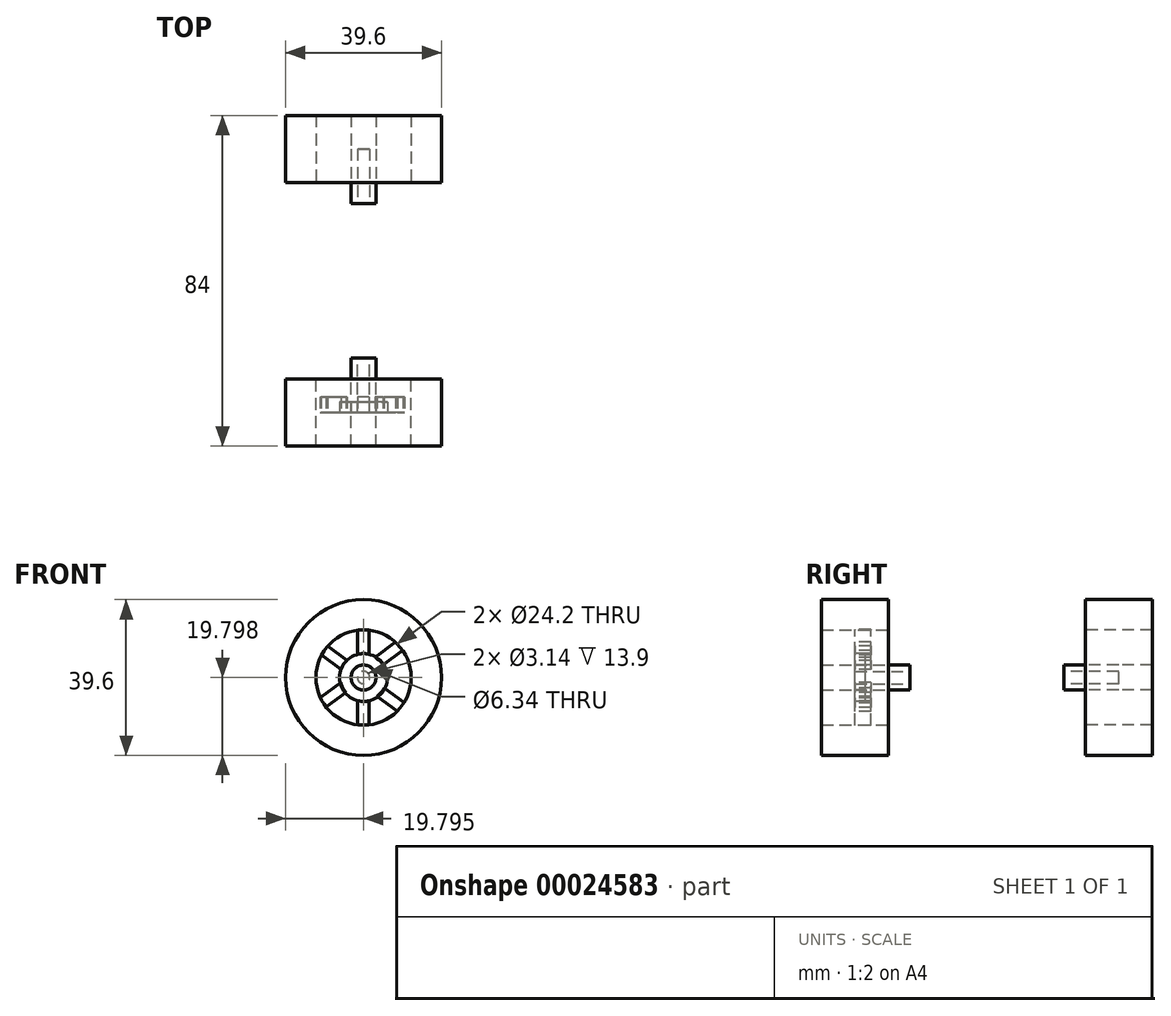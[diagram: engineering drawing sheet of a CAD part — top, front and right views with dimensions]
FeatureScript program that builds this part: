
annotation { "Feature Type Name" : "Feature", "Feature Type Description" : "" }
export const myFeature = defineFeature(function(context is Context, id is Id, definition is map)
    precondition{}
    {
        {
            var Q0;
            Q0=qCreatedBy(makeId("Front.planeOp"),FACE);
            var sketch = newSketch(context, id + "F0", { "sketchPlane" : qUnion([Q0])});
            skCircle(sketch, "E0", {"center": v(-14.5, -5.85) * mm, "radius": 3.17 * mm});
            skCircle(sketch, "E1.0", {"center": v(-14.5, -5.85) * mm, "radius": 1.57 * mm});
            skSolve(sketch);
        }
        {
            var Q0;
            Q0=makeQuery(id+"F0.imprint","IMPRINT",FACE,{"disambiguationData":[TD([[makeQuery(id+"F0.imprint","IMPRINT",EDGE,{"derivedFrom":sQuery(id+"F0.wireOp",EDGE,"E0")}),1.0]])]});
            extrude(context, id + "F1", {"entities" : qUnion([Q0]), "depth" : 9.2 * mm});
        }
        {
            var Q0;
            Q0=makeQuery(id+"F1.opExtrude","CAP_FACE",FACE,{"disambiguationData":[OSD([sQuery(id+"F0.wireOp",EDGE,"E0"),sQuery(id+"F0.wireOp",EDGE,"E1.0")])],"isStart":false});
            var sketch = newSketch(context, id + "F2", { "sketchPlane" : qUnion([Q0])});
            skCircle(sketch, "E2.0", {"center": v(-14.5, -5.85) * mm, "radius": 6.07 * mm});
            skSolve(sketch);
        }
        {
            var Q0;
            Q0=makeQuery(id+"F2.imprint","IMPRINT",FACE,{"disambiguationData":[TD([[makeQuery(id+"F2.imprint","IMPRINT",EDGE,{"derivedFrom":sQuery(id+"F2.wireOp",EDGE,"E2.0")}),1.0]])]});
            extrude(context, id + "F3", {"entities" : qUnion([Q0]), "oppositeDirection" : true, "depth" : 2.7 * mm});
        }
        {
            var Q0;
            Q0=makeQuery(id+"F3.opExtrude","CAP_FACE",FACE,{"disambiguationData":[OSD([sQuery(id+"F0.wireOp",EDGE,"E0"),sQuery(id+"F2.wireOp",EDGE,"E2.0")])],"isStart":true});
            var sketch = newSketch(context, id + "F4", { "sketchPlane" : qUnion([Q0])});
            skArc(sketch, "E3", {"start": v(-23.66, 2.2) * mm, "mid": v(-24.53, 1.09) * mm, "end": v(-25.26, -0.1) * mm});
            skLineSegment(sketch, "E4", {"start": v(-24.08, -13.4) * mm, "end": v(-19, -9.65) * mm});
            skLineSegment(sketch, "E5.0", {"start": v(-13.15, -18.05) * mm, "end": v(-13.15, -11.58) * mm});
            skLineSegment(sketch, "E6.0", {"start": v(-15.95, -18.05) * mm, "end": v(-15.95, -11.55) * mm});
            skLineSegment(sketch, "E7.0", {"start": v(-4.11, -12.26) * mm, "end": v(-9.23, -8.47) * mm});
            skLineSegment(sketch, "E8.0", {"start": v(-5.85, -14.46) * mm, "end": v(-11.04, -10.62) * mm});
            skLineSegment(sketch, "E9.0", {"start": v(-25.55, -11.01) * mm, "end": v(-20.25, -7.1) * mm});
            skLineSegment(sketch, "E10.trimOffspring", {"start": v(-13.15, -0.13) * mm, "end": v(-13.15, 6.35) * mm});
            skLineSegment(sketch, "E11.trimOffspring", {"start": v(-11.62, -0.72) * mm, "end": v(-6.32, 3.2) * mm});
            skLineSegment(sketch, "E12.trimOffspring", {"start": v(-18.55, -1.59) * mm, "end": v(-23.7, 2.22) * mm});
            skCircle(sketch, "E13", {"center": v(-14.5, -5.85) * mm, "radius": 5.88 * mm});
            skLineSegment(sketch, "E14.trimOffspring", {"start": v(-15.95, -0.15) * mm, "end": v(-15.95, 6.35) * mm});
            skLineSegment(sketch, "E15.trimOffspring", {"start": v(-20.06, -3.95) * mm, "end": v(-25.36, -0.03) * mm});
            skLineSegment(sketch, "E16.trimOffspring", {"start": v(-9.55, -2.67) * mm, "end": v(-4.46, 1.1) * mm});
            skArc(sketch, "E17.trimOffspring", {"start": v(-13.15, 6.27) * mm, "mid": v(-14.55, 6.35) * mm, "end": v(-15.95, 6.26) * mm});
            skArc(sketch, "E18.trimOffspring", {"start": v(-4.46, 1.1) * mm, "mid": v(-5.33, 2.2) * mm, "end": v(-6.32, 3.2) * mm});
            skArc(sketch, "E19.trimOffspring", {"start": v(-5.85, -14.46) * mm, "mid": v(-4.92, -13.4) * mm, "end": v(-4.11, -12.26) * mm});
            skArc(sketch, "E20.trimOffspring", {"start": v(-15.95, -17.97) * mm, "mid": v(-14.55, -18.05) * mm, "end": v(-13.15, -17.98) * mm});
            skArc(sketch, "E21.trimOffspring", {"start": v(-25.55, -11.01) * mm, "mid": v(-24.88, -12.25) * mm, "end": v(-24.08, -13.4) * mm});
            skSolve(sketch);
        }
        {
            var Q0;
            {var subQ0=sQuery(id+"F4.wireOp",EDGE,"E17.trimOffspring");Q0=makeQuery(id+"F4.imprint","IMPRINT",FACE,{"disambiguationData":[TD([[makeQuery(id+"F4.imprint","IMPRINT",EDGE,{"derivedFrom":subQ0}),1.0]])]});}
            var Q1;
            {var subQ2=sQuery(id+"F4.wireOp",EDGE,"E11.trimOffspring");Q1=makeQuery(id+"F4.imprint","IMPRINT",FACE,{"disambiguationData":[TD([[makeQuery(id+"F4.imprint","IMPRINT",EDGE,{"derivedFrom":subQ2}),-1.0]])]});}
            var Q2;
            {var subQ2=sQuery(id+"F4.wireOp",EDGE,"E7.0");Q2=makeQuery(id+"F4.imprint","IMPRINT",FACE,{"disambiguationData":[TD([[makeQuery(id+"F4.imprint","IMPRINT",EDGE,{"derivedFrom":subQ2}),1.0]])]});}
            var Q3;
            {var subQ0=sQuery(id+"F4.wireOp",EDGE,"E20.trimOffspring");Q3=makeQuery(id+"F4.imprint","IMPRINT",FACE,{"disambiguationData":[TD([[makeQuery(id+"F4.imprint","IMPRINT",EDGE,{"derivedFrom":subQ0}),1.0]])]});}
            var Q4;
            {var subQ3=sQuery(id+"F4.wireOp",EDGE,"E3");Q4=makeQuery(id+"F4.imprint","IMPRINT",FACE,{"disambiguationData":[TD([[makeQuery(id+"F4.imprint","IMPRINT",EDGE,{"derivedFrom":subQ3}),1.0]])]});}
            var Q5;
            {var subQ2=sQuery(id+"F4.wireOp",EDGE,"E4");Q5=makeQuery(id+"F4.imprint","IMPRINT",FACE,{"disambiguationData":[TD([[makeQuery(id+"F4.imprint","IMPRINT",EDGE,{"derivedFrom":subQ2}),1.0]])]});}
            extrude(context, id + "F5", {"entities" : qUnion([Q0, Q1, Q2, Q3, Q4, Q5]), "oppositeDirection" : true, "depth" : 4 * mm});
        }
        {
            var Q0;
            Q0=makeQuery(id+"F1.opExtrude","CAP_FACE",FACE,{"disambiguationData":[OSD([sQuery(id+"F0.wireOp",EDGE,"E0"),sQuery(id+"F0.wireOp",EDGE,"E1.0")])],"isStart":false});
            var sketch = newSketch(context, id + "F6", { "sketchPlane" : qUnion([Q0])});
            skCircle(sketch, "E22", {"center": v(-14.5, -5.85) * mm, "radius": 12.1 * mm});
            skCircle(sketch, "E23.0", {"center": v(-14.5, -5.85) * mm, "radius": 19.8 * mm});
            skSolve(sketch);
        }
        {
            var Q0;
            Q0=makeQuery(id+"F6.imprint","IMPRINT",FACE,{"disambiguationData":[TD([[makeQuery(id+"F6.imprint","IMPRINT",EDGE,{"derivedFrom":sQuery(id+"F6.wireOp",EDGE,"E22")}),-1.0]])]});
            extrude(context, id + "F7", {"entities" : qUnion([Q0]), "endBound" : BoundingType.SYMMETRIC, "depth" : 17 * mm});
        }
        {
            var Q0;
            Q0=makeQuery(id+"F1.opExtrude","CAP_FACE",FACE,{"disambiguationData":[OSD([sQuery(id+"F0.wireOp",EDGE,"E0"),sQuery(id+"F0.wireOp",EDGE,"E1.0")])],"isStart":true});
            extrude(context, id + "F8", {"entities" : qUnion([Q0]), "operationType" : NewBodyOperationType.ADD, "depth" : 4.7 * mm});
        }
        {
            var Q0;
            Q0=makeQuery(id+"F1.opExtrude","CAP_FACE",FACE,{"disambiguationData":[OSD([sQuery(id+"F0.wireOp",EDGE,"E0"),sQuery(id+"F0.wireOp",EDGE,"E1.0")])],"isStart":false});
            var sketch = newSketch(context, id + "F9", { "sketchPlane" : qUnion([Q0])});
            skCircle(sketch, "E24", {"center": v(-14.5, -5.85) * mm, "radius": 3.16 * mm});
            skSolve(sketch);
        }
        {
            var Q0;
            Q0=qSketchRegion(id+"F9",true);
            var Q1;
            Q1=makeQuery(id+"F7.opExtrude","CAP_FACE",FACE,{"disambiguationData":[OSD([sQuery(id+"F6.wireOp",EDGE,"E22"),sQuery(id+"F6.wireOp",EDGE,"E23.0")])],"isStart":false});
            extrude(context, id + "F10", {"entities" : qUnion([Q0]), "operationType" : NewBodyOperationType.ADD, "endBound" : BoundingType.UP_TO_SURFACE, "endBoundEntityFace" : qUnion([Q1]), "depth" : 25 * mm});
        }
        {
            var Q0;
            Q0=makeQuery(id+"F10.opExtrude","CAP_FACE",FACE,{"disambiguationData":[OSD([sQuery(id+"F9.wireOp",EDGE,"E24")])],"isStart":false});
            extrude(context, id + "F11", {"entities" : qUnion([Q0]), "operationType" : NewBodyOperationType.ADD, "oppositeDirection" : true, "depth" : 3 * mm});
        }
        {
            var Q0;
            Q0=makeQuery(id+"F7.opExtrude","SWEPT_BODY",BODY,{"disambiguationData":[OSD([sQuery(id+"F6.wireOp",EDGE,"E22"),sQuery(id+"F6.wireOp",EDGE,"E23.0")])]});
            var Q1;
            Q1=makeQuery(id+"F1.opExtrude","SWEPT_BODY",BODY,{"disambiguationData":[OSD([sQuery(id+"F0.wireOp",EDGE,"E0"),sQuery(id+"F0.wireOp",EDGE,"E1.0")])]});
            var Q2;
            Q2=makeQuery(id+"F7.opExtrude","CAP_FACE",FACE,{"disambiguationData":[OSD([sQuery(id+"F6.wireOp",EDGE,"E22"),sQuery(id+"F6.wireOp",EDGE,"E23.0")])],"isStart":true});
            mirror(context, id + "F12", {"entities" : qUnion([Q0, Q1]), "mirrorPlane" : qUnion([Q2])});
        }
        {
            var Q0;
            Q0=makeQuery(id+"F12.opPattern","COPY",BODY,{"derivedFrom":makeQuery(id+"F1.opExtrude","SWEPT_BODY",BODY,{"disambiguationData":[OSD([sQuery(id+"F0.wireOp",EDGE,"E0"),sQuery(id+"F0.wireOp",EDGE,"E1.0")])]}),"instanceName":"1"});
            var Q1;
            Q1=makeQuery(id+"F12.opPattern","COPY",BODY,{"derivedFrom":makeQuery(id+"F7.opExtrude","SWEPT_BODY",BODY,{"disambiguationData":[OSD([sQuery(id+"F6.wireOp",EDGE,"E22"),sQuery(id+"F6.wireOp",EDGE,"E23.0")])]}),"instanceName":"1"});
            var Q2;
            Q2=makeQuery(id+"F12.opPattern","COPY",FACE,{"derivedFrom":makeQuery(id+"F10.opExtrude","SWEPT_FACE",FACE,{"disambiguationData":[OSD([sQuery(id+"F9.wireOp",EDGE,"E24")])]}),"instanceName":"1"});
            transform(context, id + "F13", {"entities" : qUnion([Q0, Q1]), "transformType" : TransformType.TRANSLATION_DISTANCE, "transformDirection" : qUnion([Q2]), "distance" : 50 * mm, "oppositeDirection" : true, "makeCopy" : false});
        }
    });
